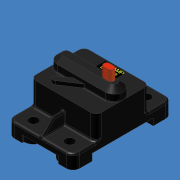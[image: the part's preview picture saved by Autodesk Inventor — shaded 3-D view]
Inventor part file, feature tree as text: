
AUTODESK INVENTOR PART (.ipt)
format: ipt  version: 2012 (Build 160160000, 160)  size: 368,128 bytes
history: native  units: mm (DEFAULTED — no unit token found)
features: sketch x10, extrude x7, fillet x7, mirror x3, chamfer x2, hole x1, emboss x1, other x1
ambient origin geometry x8: Origin, YZ Plane, XZ Plane, XY Plane, X Axis, Y Axis, Z Axis, Center Point
bodies: Solid1 (feature_tree)
feature tree (32):
  extrude  "Extrusion1"  Depth=73.406mm
  fillet  "Fillet1"  Radius=24.13mm
  extrude  "Extrusion2"  Depth=5.08mm TaperAngle=0.0deg
  fillet  "Fillet2"  Radius=5.08mm
  hole  "Hole1"  [1 undecoded]
  extrude  "Extrusion3"  Depth=10.795mm
  mirror  "Mirror3"
  mirror  "Mirror4"
  extrude  "Extrusion4"  Depth=14.224mm
  fillet  "Fillet3"  Radius=14.224mm
  chamfer  "Chamfer1"  Distance=5.08mm
  extrude  "Button"  Depth=8.89mm TaperAngle=0.0deg
  fillet  "Fillet4"  Radius=6.477mm
  fillet  "Fillet7"  Radius=3.81mm
  extrude  "Extrusion6"  Depth=7.62mm
  chamfer  "Chamfer2"  Distance=7.62mm
  fillet  "Fillet5"  Radius=2.159mm
  mirror  "Mirror5"
  fillet  "Fillet6"  Radius=2.54mm
  extrude  "Extrusion8"  Depth=8.89mm TaperAngle=0.0deg
  emboss  "Emboss1"
  sketch  "Sketch1"  dims[d0=48.26mm d1=73.406mm d2=24.13mm]
  sketch  "Sketch2"  dims[d3=36.703mm d4=5.08mm d5=0.0mm d6=5.08mm]
  sketch  "Sketch3"  dims[d7=39.37mm d8=17.526mm d9=0.0mm]
  sketch  "Sketch5"  dims[d10=3.81mm d11=10.795mm]
  sketch  "Sketch6"  dims[d12=8.382mm]
  sketch  "Sketch7"  dims[d13=6.604mm d14=12.7mm d15=9.525mm d16=6.35mm d17=14.3117mm d18=19.05mm d19=20.594885mm d20=14.224mm d21=14.224mm d23=5.08mm d24=0.0mm]
  sketch  "Sketch8"  dims[d25=12.954mm d26=8.89mm d27=0.0mm d28=6.477mm d29=3.81mm d30=3.81mm]
  sketch  "Sketch9"  dims[d31=4.318mm d32=7.62mm]
  other  "Image1"
  sketch  "Sketch10"  dims[d33=2.159mm d34=7.62mm d35=0.0mm d36=2.159mm d37=2.54mm]
  sketch  "Sketch12"  dims[d38=1.27mm d39=8.89mm d40=0.0mm d41=8.89mm d42=8.89mm d43=1.27mm d44=1.27mm d45=0.635mm d46=1.27mm d47=45.0deg d48=45.0deg d56=5.08mm d57=0.0mm d58=2.54mm d59=0.0mm]
note: 1 required parameter value undecoded (feature->parameter linkage not recoverable at this tier; creation-order binding heuristic only, values carry confidence <= 0.55)
